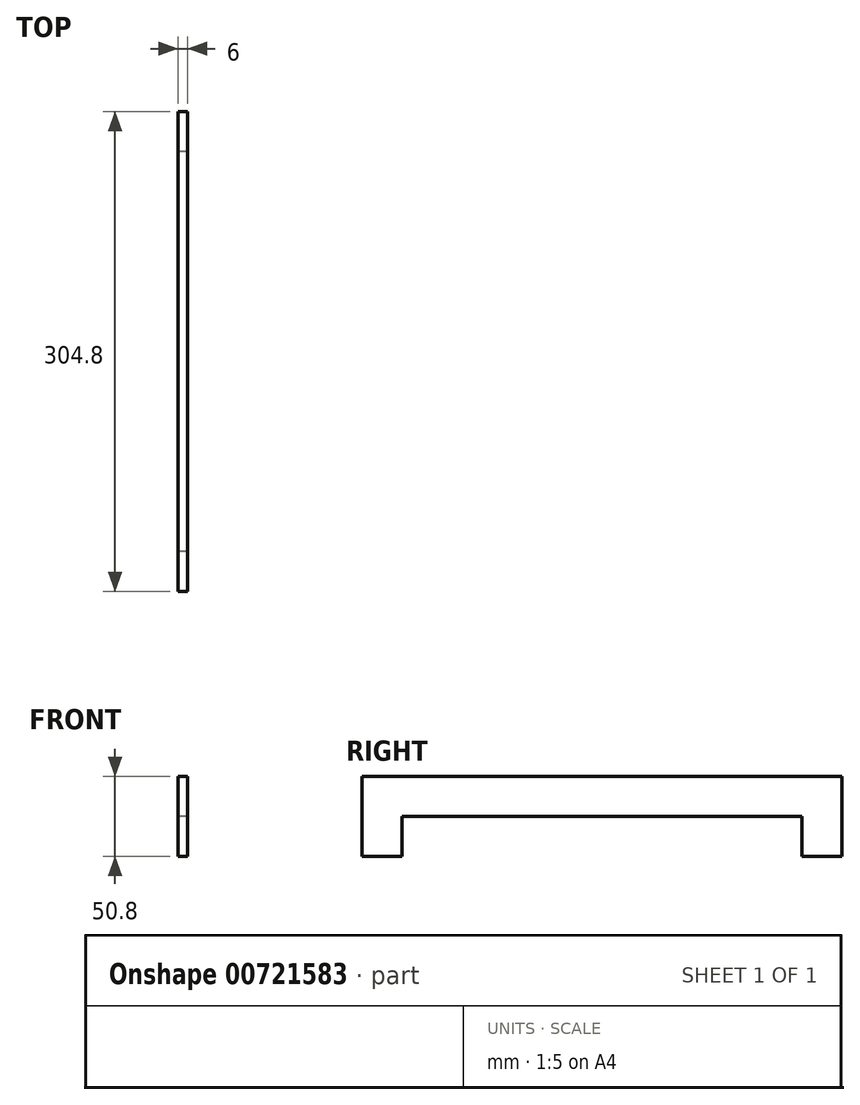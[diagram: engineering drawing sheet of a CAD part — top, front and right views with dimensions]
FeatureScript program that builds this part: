
annotation { "Feature Type Name" : "Feature", "Feature Type Description" : "" }
export const myFeature = defineFeature(function(context is Context, id is Id, definition is map)
    precondition{}
    {
        {
            var Q0;
            Q0=qCreatedBy(makeId("Right.planeOp"),FACE);
            var sketch = newSketch(context, id + "F0", { "sketchPlane" : qUnion([Q0])});
            skLineSegment(sketch, "E0.top", {"start": v(152.4, 25.4) * mm, "end": v(-152.4, 25.4) * mm});
            skLineSegment(sketch, "E0.left", {"start": v(152.4, -25.4) * mm, "end": v(152.4, 25.4) * mm});
            skLineSegment(sketch, "E0.right", {"start": v(-152.4, -25.4) * mm, "end": v(-152.4, 25.4) * mm});
            skPoint(sketch, "E0.middle", {"position": v(0, 0) * mm});
            skLineSegment(sketch, "E1", {"start": v(152.4, 25.4) * mm, "end": v(152.4, -25.4) * mm});
            skLineSegment(sketch, "E2", {"start": v(127, -25.4) * mm, "end": v(127, 0) * mm});
            skLineSegment(sketch, "E3", {"start": v(127, 0) * mm, "end": v(-127, 0) * mm});
            skLineSegment(sketch, "E4", {"start": v(-127, 0) * mm, "end": v(-127, -25.4) * mm});
            skLineSegment(sketch, "E5", {"start": v(-127, -25.4) * mm, "end": v(-152.4, -25.4) * mm});
            skLineSegment(sketch, "E6", {"start": v(127, -25.4) * mm, "end": v(152.4, -25.4) * mm});
            skSolve(sketch);
        }
        {
            var Q0;
            Q0=makeQuery(id+"F0.imprint","IMPRINT",FACE,{"disambiguationData":[TD([[makeQuery(id+"F0.imprint","IMPRINT",EDGE,{"derivedFrom":sQuery(id+"F0.wireOp",EDGE,"E0.top")}),1.0]])]});
            extrude(context, id + "F1", {"entities" : qUnion([Q0]), "depth" : 6 * mm, "offsetDistance" : 25.4 * mm, "symmetric" : true});
        }
    });
